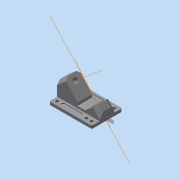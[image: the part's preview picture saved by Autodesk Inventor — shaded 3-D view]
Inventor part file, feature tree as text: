
AUTODESK INVENTOR PART (.ipt)
format: ipt  version: 2015 SP1 (Build 190203100, 203)  size: 343,040 bytes
history: native  units: in
note: dims shown in document units (in); Inventor stores cm internally (conversion verified against a paired STEP export)
features: sketch x15, extrude x13, projected_geometry x9, plane x3, chamfer x3, other x3, mirror x1, draft x1, fillet x1
ambient origin geometry x8: Origin, YZ Plane, XZ Plane, XY Plane, X Axis, Y Axis, Z Axis, Center Point
bodies: Solid1 (feature_tree)
feature tree (49):
  extrude  "Extrusion1"  Depth=2.2in
  plane  "Work Plane1"
  extrude  "Extrusion2"  Depth=0.21in TaperAngle=0.0deg
  extrude  "Extrusion3"  Depth=0.205in
  mirror  "Mirror1"
  extrude  "Extrusion4"  Depth=0.278in
  extrude  "Extrusion5"  Depth=0.3in
  extrude  "Extrusion6"  Depth=0.45in
  chamfer  "Chamfer1"  Distance=0.05in
  extrude  "Extrusion7"  Depth=0.57in
  chamfer  "Chamfer2"  Distance=0.15in
  other  "Work Axis1"
  extrude  "Extrusion8"  Depth=1.06in TaperAngle=0.0deg
  extrude  "Extrusion9"  Depth=0.75in
  chamfer  "Chamfer3"  Distance=0.75in
  extrude  "Extrusion10"  Depth=0.25in
  draft  "FaceDraft5"
  extrude  "Extrusion11"  Depth=0.5in TaperAngle=0.0deg
  sketch  "Sketch14"  dims[d42=0.5in d43=0.5in d44=0.0in]
  sketch  "Sketch15"  dims[d46=0.25in d47=0.125in d48=45.0deg d49=1.46in d50=1.3in d51=0.0in]
  extrude  "Extrusion13"  Depth=1.46in
  fillet  "Fillet2"  Radius=1.3in
  other  "Work Axis2"
  extrude  "Extrusion14"  Depth=0.2in
  plane  "Work Plane4"
  sketch  "Sketch18"  dims[d54=0.3436in d55=1.3in d56=0.0in d57=0.2in d58=0.125in d59=45.0deg d63=0.66in d64=0.125in d65=0.4in d66=0.0in d67=0.3436in d68=0.37in d69=0.4in d70=0.0in d71=1.1in d72=0.76in d73=0.0in d74=0.11in d75=0.8in d76=0.8933in d77=90.0deg d78=0.4in d79=0.4in d82=0.76in d83=0.0in d84=0.135in d85=1.08in d86=0.75in d87=0.05in d88=0.05in d89=0.5in d90=0.03in d91=0.0in d92=0.0137in d93=0.8125in d94=0.8125in d95=0.8125in d96=2.5in d97=2.125in]
  other  "Work Axis3"
  sketch  "Sketch1"  dims[d0=3.074in d1=2.2in]
  sketch  "Sketch2"  dims[d2=0.1in d3=0.21in d4=0.0in]
  sketch  "Sketch3"  dims[d5=0.205in d6=0.205in]
  plane  "Work Plane2"
  sketch  "Sketch4"  dims[d7=0.205in d8=0.278in]
  projected_geometry  "Projected Loop1"
  sketch  "Sketch5"  dims[d14=0.21in d15=0.0in d16=0.3in]
  projected_geometry  "Projected Loop2"
  sketch  "Sketch8"  dims[d17=0.45in d18=0.45in]
  projected_geometry  "Projected Loop4"
  sketch  "Sketch9"  dims[d19=0.0in d20=0.05in d21=0.0in]
  sketch  "Sketch10"  dims[d22=0.57in d23=0.57in d24=0.15in d25=0.0in]
  projected_geometry  "Projected Loop5"
  sketch  "Sketch11"  dims[d26=1.06in d27=0.65in d28=0.0in]
  projected_geometry  "Projected Loop6"
  sketch  "Sketch12"  dims[d34=0.3436in d35=0.3436in d36=0.75in d37=0.0in]
  projected_geometry  "Projected Loop7"
  sketch  "Sketch13"  dims[d38=0.25in d39=0.125in d40=45.0deg d41=0.7in]
  projected_geometry  "Projected Loop8"
  projected_geometry  "Projected Loop9"
  projected_geometry  "Projected Loop10"
  sketch  "Sketch17"  dims[d52=0.2in d53=0.3436in]
